# Revit family: ASSA_ABLOY_SW200i_01
name_source: partatom
category: Doors
units: mm (PartAtom-declared; Revit-internal decimal feet)

## family parameters
Always vertical = Yes
Cut with Voids When Loaded = No
Host = Wall
OmniClass Number = 23.30.10.00
OmniClass Title = Doors
Room Calculation Point = No
Shared = No

## types (2) — shared parameters
BIMobject category = Swing Doors
Bottom Profile Height = Fold Leaf1 : 0'  4"
Bottom Profile Option 01 = Fold Leaf1 : 0'  4"
Bottom Profile Option 02 = Fold Leaf1 : 0'  7"
Bottom Profile Option 03 = Fold Leaf1 : 0'  10"
Bottom Profile Option 04 = Fold Leaf1 : 0'  12"
Brass Polished Finish = Brass, Polished
Brass Satin Finish = Brass, Satin
Clear Anodized = Clear Anodized
Dark Bronze Anodized = Dark Bronze Anodized
Depth = 0.00
Edition number = 1
Frame Material = Clear Anodized
Function = Interior
Gap = 0' - 0 1/4"
Glass = Glass
Height = 7' - 5 1/2"
IFC Classification = Door
Leaf Height = 6' - 10 7/8"
Manufacturer name = Besam-North America
Material main = Aluminium
Nominal height = 0.00
Nominal width = 0.00
Product SKU = SW200i_fold
Product data url = http://besam-na.bimobject.com
Product family = ICU
Product group = Fold
QR code = http://besam-na.bimobject.com
Rough Height = 9' - 0"
Rubber = Rubber, Black
Stainless Steel Polished Finish = Stainless Steel, Polished
Stainless Steel Satin Finish = Stainless Steel, Satin
Technical description = http://www.besam.us
Top Profile Height = 0' - 4"
Transom Height = 1' - 6 1/4"
UNSPSC Code = 30171511
Uniclass 1.4 Code = L81323
Uniclass 1.4 Description = Swings
Wall Closure = By host
Weight Net (Kg) = 0

## per-type parameters (varying)
| type | Leaf Width | Rough Width | Width |
| OFW 3' 9 1/2'' | 1' - 7 25/32" | 3' - 10" | 3' - 9 1/2" |
| OFW 4' 3 1/2'' | 1' - 10 25/32" | 4' - 4" | 4' - 3 1/2" |

## geometry (parser evidence)
native form markers: Sweep x87
no freeform markers — native parametric forms only
